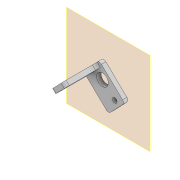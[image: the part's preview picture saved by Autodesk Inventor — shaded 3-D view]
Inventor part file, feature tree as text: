
AUTODESK INVENTOR PART (.ipt)
format: ipt  version: 2022 (Build 260153000, 153)  size: 142,336 bytes
history: native  units: mm
features: reference x11, extrude x3, sketch x3, other x3, plane x2, fillet x1, projected_geometry x1
ambient origin geometry x8: Origin, YZ Plane, XZ Plane, XY Plane, X Axis, Y Axis, Z Axis, Center Point
bodies: Body1 (feature_tree)
feature tree (24):
  plane  "Arbeitsebene3"
  extrude  "Extrusion4"  Depth=16.0mm
  sketch  "Skizze5"  dims[d17=24.0mm d18=3.0mm d19=0.0mm]
  plane  "Arbeitsebene4"
  extrude  "Extrusion5"  Depth=3.0mm TaperAngle=0.0deg
  extrude  "Extrusion6"  Depth=3.0mm TaperAngle=0.0deg
  fillet  "Rundung1"  Radius=10.0mm
  sketch  "Skizze4"  dims[d15=0.0mm d16=16.0mm]
  reference  "Referenz7"
  reference  "Referenz8"
  reference  "Referenz9"
  reference  "Referenz10"
  reference  "Referenz11"
  reference  "Referenz12"
  reference  "Referenz13"
  reference  "Referenz14"
  reference  "Referenz15"
  projected_geometry  "Projizierte Kontur1"
  sketch  "Skizze6"  dims[d20=3.0mm d21=3.0mm d22=0.0mm d23=10.0mm d24=0.0mm d25=2.0mm d26=8.0mm d27=3.2mm d28=0.9mm d29=0.9mm]
  reference  "Referenz16"
  reference  "Referenz17"
  other  "Baugruppe1"
  other  "IM_Matchboxscope_base_old:1"
  other  "00_Microlinearmotor:1"
